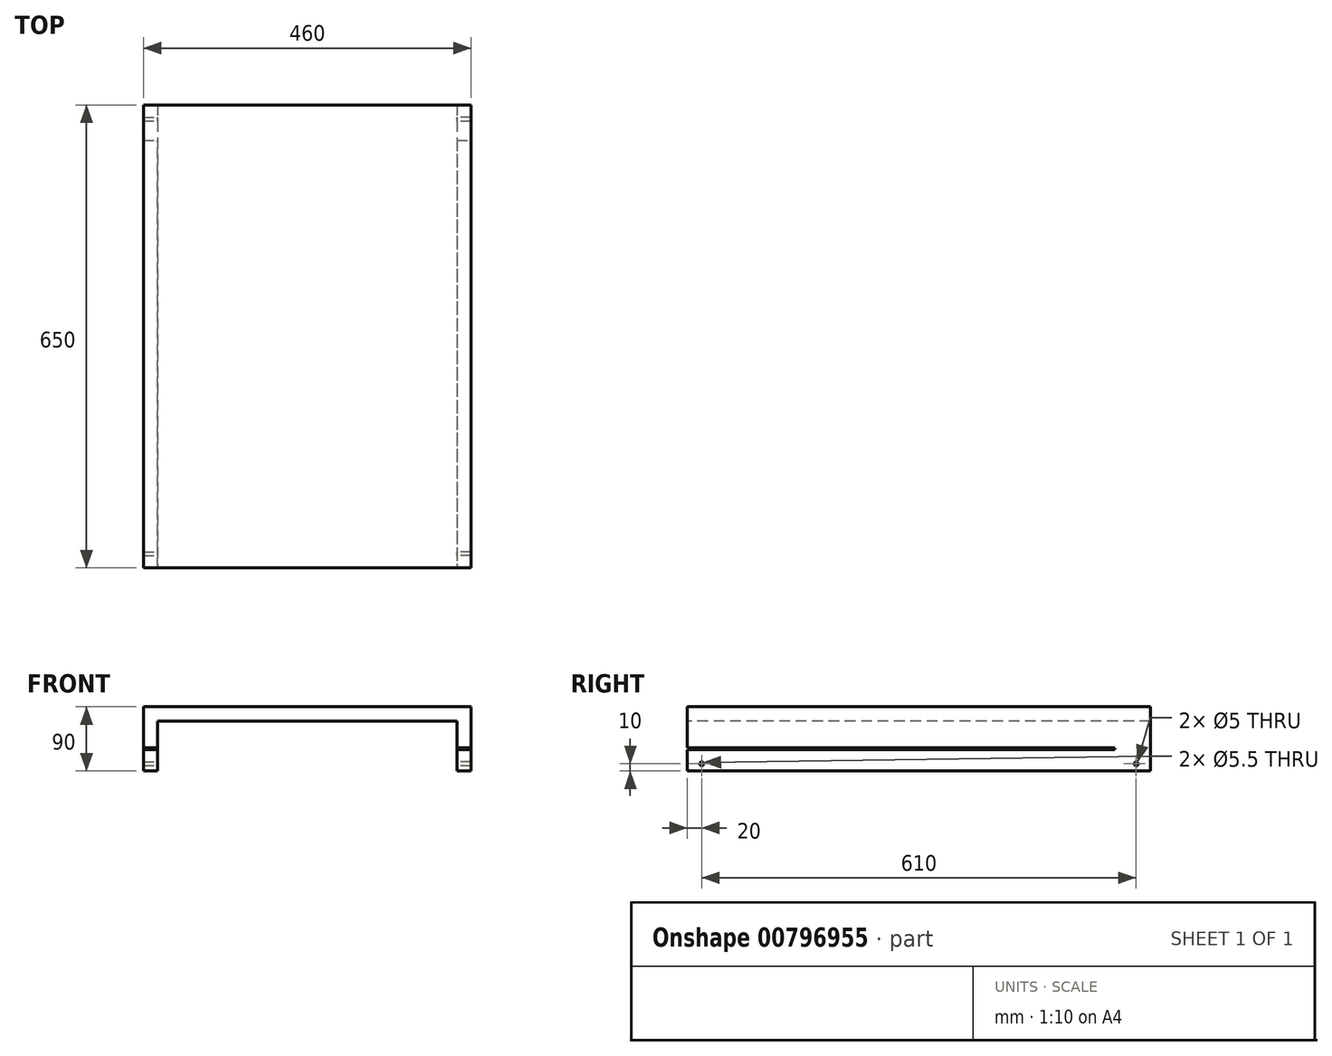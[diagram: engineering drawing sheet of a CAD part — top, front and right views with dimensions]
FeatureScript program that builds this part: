
annotation { "Feature Type Name" : "Feature", "Feature Type Description" : "" }
export const myFeature = defineFeature(function(context is Context, id is Id, definition is map)
    precondition{}
    {
        {
            var Q0;
            Q0=qCreatedBy(makeId("Top.planeOp"),FACE);
            var sketch = newSketch(context, id + "F0", { "sketchPlane" : qUnion([Q0])});
            skLineSegment(sketch, "E0.bottom", {"start": v(230, -325) * mm, "end": v(-230, -325) * mm});
            skLineSegment(sketch, "E0.top", {"start": v(230, 325) * mm, "end": v(-230, 325) * mm});
            skLineSegment(sketch, "E0.left", {"start": v(230, -325) * mm, "end": v(230, 325) * mm});
            skLineSegment(sketch, "E0.right", {"start": v(-230, -325) * mm, "end": v(-230, 325) * mm});
            skPoint(sketch, "E0.middle", {"position": v(0, 0) * mm});
            skSolve(sketch);
        }
        {
            var Q0;
            Q0=makeQuery(id+"F0.imprint","IMPRINT",FACE,{"disambiguationData":[TD([[makeQuery(id+"F0.imprint","IMPRINT",EDGE,{"derivedFrom":sQuery(id+"F0.wireOp",EDGE,"E0.bottom")}),-1.0]])]});
            extrude(context, id + "F1", {"entities" : qUnion([Q0]), "depth" : 90 * mm, "offsetDistance" : 25 * mm});
        }
        {
            var Q0;
            Q0=makeQuery(id+"F1.opExtrude","SWEPT_FACE",FACE,{"disambiguationData":[OSD([sQuery(id+"F0.wireOp",EDGE,"E0.bottom")])]});
            var sketch = newSketch(context, id + "F2", { "sketchPlane" : qUnion([Q0])});
            skLineSegment(sketch, "E1", {"start": v(-210, 0) * mm, "end": v(-210, 70) * mm});
            skLineSegment(sketch, "E2", {"start": v(-210, 70) * mm, "end": v(210, 70) * mm});
            skLineSegment(sketch, "E3", {"start": v(210, 70) * mm, "end": v(210, 0) * mm});
            skSolve(sketch);
        }
        {
            var Q0;
            {var subQ0=sQuery(id+"F2.wireOp",EDGE,"E1");Q0=makeQuery(id+"F2.imprint","IMPRINT",FACE,{"disambiguationData":[TD([[makeQuery(id+"F2.imprint","IMPRINT",EDGE,{"derivedFrom":subQ0}),-1.0]])]});}
            var Q1;
            Q1=sQuery(id+"F2.wireOp",EDGE,"E2");
            var Q2;
            Q2=sQuery(id+"F2.wireOp",EDGE,"E3");
            var Q3;
            Q3=sQuery(id+"F2.wireOp",EDGE,"E1");
            extrude(context, id + "F3", {"entities" : qUnion([Q0]), "operationType" : NewBodyOperationType.REMOVE, "surfaceEntities" : qUnion([Q1, Q2, Q3]), "endBound" : BoundingType.THROUGH_ALL, "oppositeDirection" : true, "depth" : 25 * mm, "offsetDistance" : 25 * mm});
        }
        {
            var Q0;
            Q0=makeQuery(id+"F1.opExtrude","SWEPT_FACE",FACE,{"disambiguationData":[OSD([sQuery(id+"F0.wireOp",EDGE,"E0.left")])]});
            var sketch = newSketch(context, id + "F4", { "sketchPlane" : qUnion([Q0])});
            skLineSegment(sketch, "E4", {"start": v(-325, 32.5) * mm, "end": v(275, 32.5) * mm});
            skLineSegment(sketch, "E5", {"start": v(-325, 30) * mm, "end": v(275, 30) * mm});
            skLineSegment(sketch, "E6", {"start": v(275, 32.5) * mm, "end": v(275, 30) * mm});
            skSolve(sketch);
        }
        {
            var Q0;
            {var subQ0=sQuery(id+"F4.wireOp",EDGE,"E4");Q0=makeQuery(id+"F4.imprint","IMPRINT",FACE,{"disambiguationData":[TD([[makeQuery(id+"F4.imprint","IMPRINT",EDGE,{"derivedFrom":subQ0}),-1.0]])]});}
            extrude(context, id + "F5", {"entities" : qUnion([Q0]), "operationType" : NewBodyOperationType.REMOVE, "endBound" : BoundingType.THROUGH_ALL, "oppositeDirection" : true, "depth" : 25 * mm, "offsetDistance" : 25 * mm});
        }
        {
            var Q0;
            Q0=makeQuery(id+"F3.boolean.opBoolean","COPY",FACE,{"derivedFrom":makeQuery(id+"F3.opExtrude","SWEPT_FACE",FACE,{"disambiguationData":[OSD([sQuery(id+"F2.wireOp",EDGE,"E1")])]})});
            var sketch = newSketch(context, id + "F6", { "sketchPlane" : qUnion([Q0])});
            skLineSegment(sketch, "E7", {"start": v(-325, 10) * mm, "end": v(325, 10) * mm, "construction": true});
            skLineSegment(sketch, "E8", {"start": v(-305, 30) * mm, "end": v(-305, 0) * mm, "construction": true});
            skPoint(sketch, "E9", {"position": v(-305, 10) * mm});
            skLineSegment(sketch, "E10", {"start": v(305, 30) * mm, "end": v(305, 0) * mm, "construction": true});
            skPoint(sketch, "E11", {"position": v(305, 10) * mm});
            skSolve(sketch);
        }
        {
            var Q0;
            Q0=sQuery(id+"F6.wireOp",VERTEX,"E9");
            var Q1;
            Q1=sQuery(id+"F6.wireOp",VERTEX,"E11");
            var Q2;
            Q2=makeQuery(id+"F1.opExtrude","SWEPT_BODY",BODY,{"disambiguationData":[OSD([sQuery(id+"F0.wireOp",EDGE,"E0.bottom"),sQuery(id+"F0.wireOp",EDGE,"E0.top"),sQuery(id+"F0.wireOp",EDGE,"E0.left"),sQuery(id+"F0.wireOp",EDGE,"E0.right")])]});
            hole(context, id + "F7", {"style" : HoleStyle.SIMPLE, "endStyle" : HoleEndStyle.THROUGH, "standardTappedOrClearance" : lookupTablePath({ "standard" : "ISO", "size" : "5", "type" : "Drilled" }), "standardBlindInLast" : lookupTablePath({ "standard" : "ISO", "size" : "5", "type" : "Drilled" }), "holeDiameter" : 5 * mm, "majorDiameter" : 5 * mm, "isTappedThrough" : true, "tappedDepth" : 12 * mm, "tapClearance" : 3, "startFromSketch" : true, "locations" : qUnion([Q0, Q1]), "scope" : qUnion([Q2])});
        }
        {
            var Q0;
            Q0=makeQuery(id+"F3.boolean.opBoolean","COPY",FACE,{"derivedFrom":makeQuery(id+"F3.opExtrude","SWEPT_FACE",FACE,{"disambiguationData":[OSD([sQuery(id+"F2.wireOp",EDGE,"E3")])]})});
            var sketch = newSketch(context, id + "F8", { "sketchPlane" : qUnion([Q0])});
            skLineSegment(sketch, "E12", {"start": v(-325, 10) * mm, "end": v(325, 10) * mm, "construction": true});
            skLineSegment(sketch, "E13", {"start": v(-305, 0) * mm, "end": v(-305, 23.26) * mm, "construction": true});
            skPoint(sketch, "E14", {"position": v(-305, 10) * mm});
            skLineSegment(sketch, "E15", {"start": v(305, 20.9) * mm, "end": v(305, 0) * mm, "construction": true});
            skPoint(sketch, "E16", {"position": v(305, 10) * mm});
            skSolve(sketch);
        }
        {
            var Q0;
            Q0=sQuery(id+"F8.wireOp",VERTEX,"E16");
            var Q1;
            Q1=sQuery(id+"F8.wireOp",VERTEX,"E14");
            var Q2;
            Q2=makeQuery(id+"F1.opExtrude","SWEPT_BODY",BODY,{"disambiguationData":[OSD([sQuery(id+"F0.wireOp",EDGE,"E0.bottom"),sQuery(id+"F0.wireOp",EDGE,"E0.top"),sQuery(id+"F0.wireOp",EDGE,"E0.left"),sQuery(id+"F0.wireOp",EDGE,"E0.right")])]});
            hole(context, id + "F9", {"style" : HoleStyle.SIMPLE, "endStyle" : HoleEndStyle.THROUGH, "standardTappedOrClearance" : lookupTablePath({ "fit" : "Normal", "standard" : "ISO", "size" : "M5", "type" : "Clearance" }), "standardBlindInLast" : lookupTablePath({ "fit" : "Standard", "standard" : "ISO", "size" : "M5", "type" : "Clearance" }), "holeDiameter" : 5.5 * mm, "majorDiameter" : 5 * mm, "isTappedThrough" : true, "tappedDepth" : 12 * mm, "tapClearance" : 3, "startFromSketch" : true, "locations" : qUnion([Q0, Q1]), "scope" : qUnion([Q2])});
        }
    });
